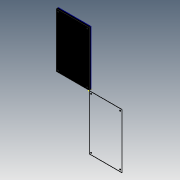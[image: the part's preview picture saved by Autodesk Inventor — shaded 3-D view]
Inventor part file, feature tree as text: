
AUTODESK INVENTOR PART (.ipt)
format: ipt  version: 2015 (Build 190159000, 159)  size: 97,792 bytes
history: native  units: mm
features: other x5, extrude x1, sketch x1, projected_geometry x1
ambient origin geometry x8: Origin, YZ Plane, XZ Plane, XY Plane, X Axis, Y Axis, Z Axis, Center Point
bodies: Body1 (feature_tree)
feature tree (8):
  other  "Blocks"
  extrude  "Extrusion2"  Depth=300.0mm
  sketch  "Sketch2"  dims[d0=180.0mm d1=300.0mm d4=5.0mm d5=10.0mm d6=10.0mm d7=90.0mm d8=150.0mm d9=10.0mm d10=0.0mm]
  other  "DXF"
  projected_geometry  "Projected Loop1"
  other  "Block1"
  other  "Block1:1"
  other  "Block1:2"
